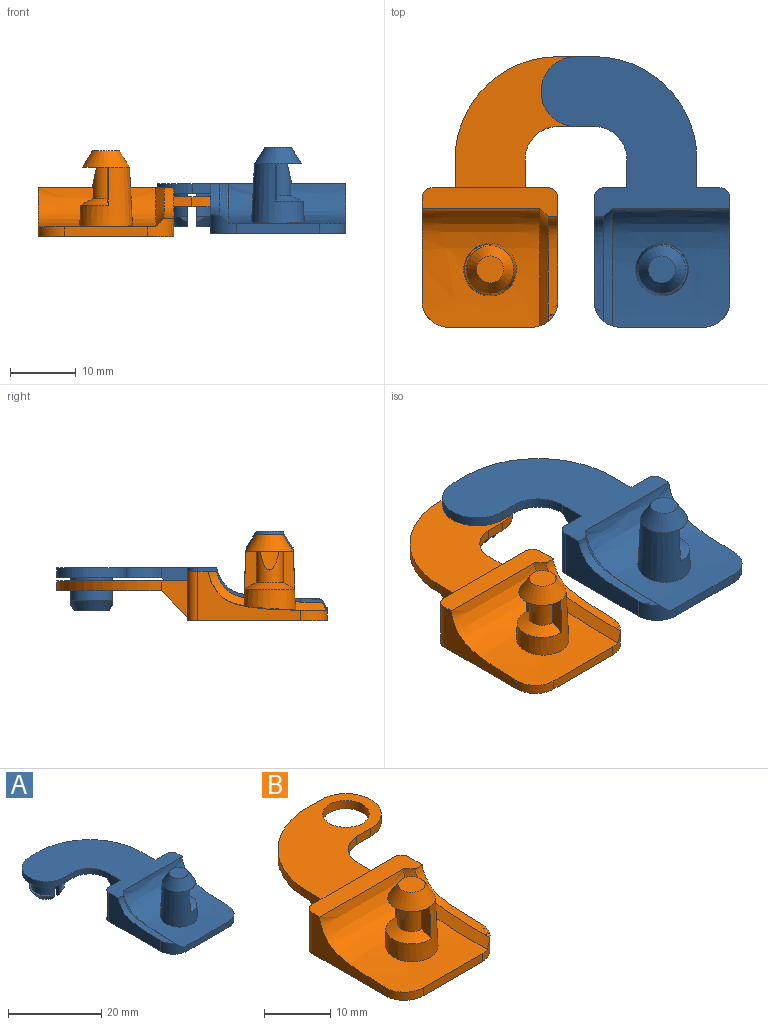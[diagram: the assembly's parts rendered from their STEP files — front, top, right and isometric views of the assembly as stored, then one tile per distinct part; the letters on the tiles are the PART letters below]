
ASSEMBLY  parts=2 mates=1
PART A: 49 faces, bbox 28.8x41.2x13.2 mm
  f0: plane 17.6x7.5mm, normal (0,1,0), area 73.7mm2, adj f11,f13,f20,f21,f24,f25,f26
  f1: extruded ~18x17.85mm, area 318.7mm2, adj f2,f11,f12,f15,f17,f18,f19
  f2: cone r=4mm half-angle=2.7deg, axis (0,0,-1), area 136.7mm2, adj f1,f4,f5,f7,f8,f9
  f3: plane 4.1x4.1mm, normal (0,0,1), area 13.2mm2, adj f4
  f4: cone r=3.58mm half-angle=31.4deg, axis (0,0,-1), area 51.7mm2, adj f2,f3
  f5: cone r=3.87mm half-angle=61.2deg, axis (0,0,-1), area 20mm2, adj f2,f6,f8,f9
  f6: cylinder r=2.05mm len=4.75mm, axis (0,0,-1), area 26.2mm2, adj f5,f7,f8,f9,f10
  f7: plane 7.15x3.89mm, normal (0,0,-1), area 15.5mm2, adj f2,f6,f8,f9,f10
  f8: plane 5.73x1.79mm, normal (1,-0.09,0), area 8.6mm2, adj f2,f5,f6,f7
  f9: plane 5.73x1.79mm, normal (1,0.09,0), area 8.6mm2, adj f2,f5,f6,f7
  f10: plane 2.92x2.84mm, normal (0.98,0,0.21), area 5.9mm2, adj f6,f7
  f11: plane 28.63x24.28mm, normal (0,0,1), area 356.6mm2, adj f0,f1,f14,f15,f16,f17,f20,f21
  f12: plane 12.6x1.5mm, normal (0,-1,0), area 18.9mm2, adj f1,f13,f18,f19
  f13: plane 21.15x20.6mm, normal (0,0,-1), area 427.9mm2, adj f0,f12,f14,f15,f18,f19,f20,f21
  f14: plane 15.65x7.5mm, normal (-1,0,0), area 66.4mm2, adj f11,f13,f16,f19,f21
  f15: plane 15.73x7.5mm, normal (1,0,0), area 46.4mm2, adj f1,f11,f13,f18,f20
  f16: extruded ~16.16x4.74mm, area 25.1mm2, adj f11,f14,f17,f19
  f17: bspline ~17.8x6mm, area 34.3mm2, adj f1,f11,f16,f19
  f18: cylinder r=4mm len=4mm, axis (0,0,-1), area 9.5mm2, adj f1,f12,f13,f15
  f19: cylinder r=4mm len=4mm, axis (0,0,1), area 14.9mm2, adj f1,f12,f13,f14,f16,f17
  f20: cylinder r=1.5mm len=7.5mm, axis (0,0,1), area 17.7mm2, adj f0,f11,f13,f15
  f21: cylinder r=1.5mm len=7.5mm, axis (0,0,-1), area 17.7mm2, adj f0,f11,f13,f14
  f22: cylinder r=3.25mm len=6.32mm, axis (0,0,1), area 30.4mm2, adj f28,f35,f37,f43
  f23: plane 5.29x2mm, normal (0,0,-1), area 3.2mm2, adj f35,f36,f37,f47
  f24: plane 10.6x4mm, normal (0,0.71,-0.71), area 60mm2, adj f0,f25,f26,f28
  f25: plane 5.5x4mm, normal (1,0,0), area 14mm2, adj f0,f11,f24,f29
  f26: plane 5.5x4mm, normal (-1,0,0), area 14mm2, adj f0,f11,f24,f27
  f27: cylinder r=5.01mm len=5.27mm, axis (0,0,1), area 11.8mm2, adj f11,f26,f28,f30
  f28: plane 23.63x15.87mm, normal (0,0,-1), area 233.2mm2, adj f22,f24,f27,f29,f30,f31,f32,f33
  f29: cylinder r=15.6mm len=15.87mm, axis (0,0,1), area 36.8mm2, adj f11,f25,f28,f31
  f30: plane 3x1.5mm, normal (0,-1,0), area 4.5mm2, adj f11,f27,f28,f32
  f31: plane 3x1.5mm, normal (0,1,0), area 4.5mm2, adj f11,f28,f29,f32
  f32: cylinder r=5.3mm len=10.6mm, axis (0,0,1), area 25mm2, adj f11,f28,f30,f31
  f33: cylinder r=3.25mm len=6.32mm, axis (0,0,1), area 30.4mm2, adj f28,f38,f40,f46
  f34: plane 5.29x2mm, normal (0,0,-1), area 3.2mm2, adj f38,f39,f40,f48
  f35: plane 5.01x1.05mm, normal (-1,0,0), area 5mm2, adj f22,f23,f28,f36,f42,f47
  f36: cylinder r=2.25mm len=5mm, axis (0,0,-1), area 27.7mm2, adj f23,f28,f35,f37
  f37: plane 5.01x1.05mm, normal (-1,0,0), area 5mm2, adj f22,f23,f28,f36,f41,f47
  f38: plane 5.01x1.05mm, normal (1,0,0), area 5mm2, adj f28,f33,f34,f39,f45,f48
  f39: cylinder r=2.25mm len=5mm, axis (0,0,-1), area 27.7mm2, adj f28,f34,f38,f40
  f40: plane 5.01x1.05mm, normal (1,0,0), area 5mm2, adj f28,f33,f34,f39,f44,f48
  f41: plane 1.46x0.94mm, normal (0,-1,0), area 0.5mm2, adj f37,f43,f47
  f42: plane 1.46x0.94mm, normal (0,1,0), area 0.5mm2, adj f35,f43,f47
  f43: plane 6.32x3mm, normal (0,0,1), area 4mm2, adj f22,f41,f42,f47
  f44: plane 1.46x0.94mm, normal (0,1,0), area 0.5mm2, adj f40,f46,f48
  f45: plane 1.46x0.94mm, normal (0,-1,0), area 0.5mm2, adj f38,f46,f48
  f46: plane 6.32x3mm, normal (0,0,1), area 4mm2, adj f33,f44,f45,f48
  f47: cone r=2.75mm half-angle=33.7deg, axis (0,0,1), area 14.5mm2, adj f23,f35,f37,f41,f42,f43
  f48: cone r=3.75mm half-angle=33.7deg, axis (0,0,1), area 14.5mm2, adj f34,f38,f40,f44,f45,f46
PART B: 33 faces, bbox 28.6x42.1x13 mm
  f0: plane 17.6x7.5mm, normal (0,1,0), area 73.7mm2, adj f11,f13,f20,f21,f22,f23,f24,f25
  f1: extruded ~18x17.85mm, area 318.7mm2, adj f2,f11,f12,f15,f17,f18,f19
  f2: cone r=4mm half-angle=2.7deg, axis (0,0,-1), area 136.7mm2, adj f1,f4,f5,f7,f8,f9
  f3: plane 4.1x4.1mm, normal (0,0,1), area 13.2mm2, adj f4
  f4: cone r=3.58mm half-angle=31.4deg, axis (0,0,-1), area 51.7mm2, adj f2,f3
  f5: cone r=3.87mm half-angle=61.2deg, axis (0,0,-1), area 20mm2, adj f2,f6,f8,f9
  f6: cylinder r=2.05mm len=4.75mm, axis (0,0,-1), area 26.2mm2, adj f5,f7,f8,f9,f10
  f7: plane 7.15x3.89mm, normal (0,0,-1), area 15.5mm2, adj f2,f6,f8,f9,f10
  f8: plane 5.73x1.79mm, normal (-1,-0.09,0), area 8.6mm2, adj f2,f5,f6,f7
  f9: plane 5.73x1.79mm, normal (-1,0.09,0), area 8.6mm2, adj f2,f5,f6,f7
  f10: plane 2.92x2.84mm, normal (-0.98,0,0.21), area 5.9mm2, adj f6,f7
  f11: plane 20.6x4.41mm, normal (0,0,1), area 66.8mm2, adj f0,f1,f14,f15,f16,f17,f20,f21
  f12: plane 12.6x1.5mm, normal (0,-1,0), area 18.9mm2, adj f1,f13,f18,f19
  f13: plane 21.15x20.6mm, normal (0,0,-1), area 427.9mm2, adj f0,f12,f14,f15,f18,f19,f20,f21
  f14: plane 15.65x7.5mm, normal (1,0,0), area 66.4mm2, adj f11,f13,f16,f19,f21
  f15: plane 15.73x7.5mm, normal (-1,0,0), area 46.4mm2, adj f1,f11,f13,f18,f20
  f16: extruded ~15.86x4.74mm, area 25.1mm2, adj f11,f14,f17,f19
  f17: bspline ~19.03x6.2mm, area 34.1mm2, adj f1,f11,f16,f19
  f18: cylinder r=4mm len=4mm, axis (0,0,-1), area 9.5mm2, adj f1,f12,f13,f15
  f19: cylinder r=4mm len=4mm, axis (0,0,1), area 14.9mm2, adj f1,f12,f13,f14,f16,f17
  f20: cylinder r=1.5mm len=7.5mm, axis (0,0,1), area 17.7mm2, adj f0,f11,f13,f15
  f21: cylinder r=1.5mm len=7.5mm, axis (0,0,-1), area 17.7mm2, adj f0,f11,f13,f14
  f22: plane 23.63x19.87mm, normal (0,0,1), area 251.3mm2, adj f0,f24,f25,f26,f28,f29,f30,f31
  f23: plane 10.6x4mm, normal (0,0.71,-0.71), area 60mm2, adj f0,f24,f25,f27
  f24: plane 5.5x4mm, normal (-1,0,0), area 14mm2, adj f0,f22,f23,f28
  f25: plane 5.5x4mm, normal (1,0,0), area 14mm2, adj f0,f22,f23,f26
  f26: cylinder r=5.01mm len=5.27mm, axis (0,0,1), area 11.8mm2, adj f22,f25,f27,f29
  f27: plane 23.63x15.87mm, normal (0,0,-1), area 208.9mm2, adj f23,f26,f28,f29,f30,f31,f32
  f28: cylinder r=15.6mm len=15.87mm, axis (0,0,1), area 36.8mm2, adj f22,f24,f27,f30
  f29: plane 3x1.5mm, normal (0,-1,0), area 4.5mm2, adj f22,f26,f27,f31
  f30: plane 3x1.5mm, normal (0,1,0), area 4.5mm2, adj f22,f27,f28,f31
  f31: cylinder r=5.3mm len=10.6mm, axis (0,0,1), area 25mm2, adj f22,f27,f29,f30
  f32: cylinder r=3.5mm len=7mm, axis (0,0,-1), area 33mm2, adj f22,f27
PLACE A t=(16.45,-15.18,-3.85)mm
PLACE B t=(40.39,-15.18,-4.35)mm
MATE revolute B.f31 <-> A.f22  axis (0,0,1) through (53.42,11.79,0.15)mm
